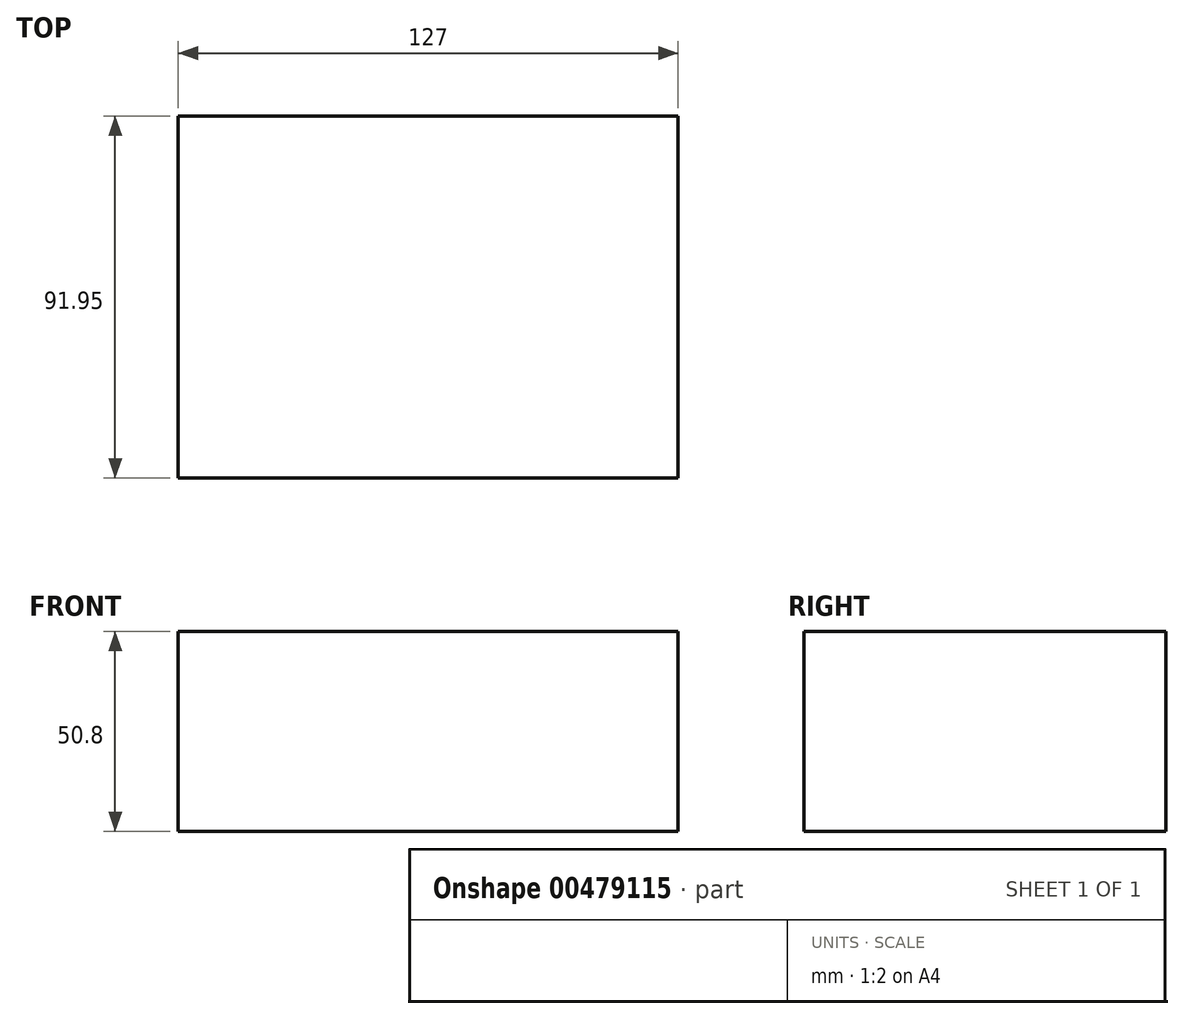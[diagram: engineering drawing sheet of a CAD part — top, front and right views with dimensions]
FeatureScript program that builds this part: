
annotation { "Feature Type Name" : "Feature", "Feature Type Description" : "" }
export const myFeature = defineFeature(function(context is Context, id is Id, definition is map)
    precondition{}
    {
        {
            var Q0;
            Q0=qCreatedBy(makeId("Front.planeOp"),FACE);
            var sketch = newSketch(context, id + "F0", { "sketchPlane" : qUnion([Q0])});
            skLineSegment(sketch, "E0.bottom", {"start": v(-63.5, 25.4) * mm, "end": v(63.5, 25.4) * mm});
            skLineSegment(sketch, "E0.top", {"start": v(-63.5, -25.4) * mm, "end": v(63.5, -25.4) * mm});
            skLineSegment(sketch, "E0.left", {"start": v(-63.5, 25.4) * mm, "end": v(-63.5, -25.4) * mm});
            skLineSegment(sketch, "E0.right", {"start": v(63.5, 25.4) * mm, "end": v(63.5, -25.4) * mm});
            skSolve(sketch);
        }
        {
            var Q0;
            Q0 = qSketchRegion(id + "F0", true);
            extrude(context, id + "F1", {"entities" : qUnion([Q0]), "depth" : 91.95 * mm});
        }
    });
